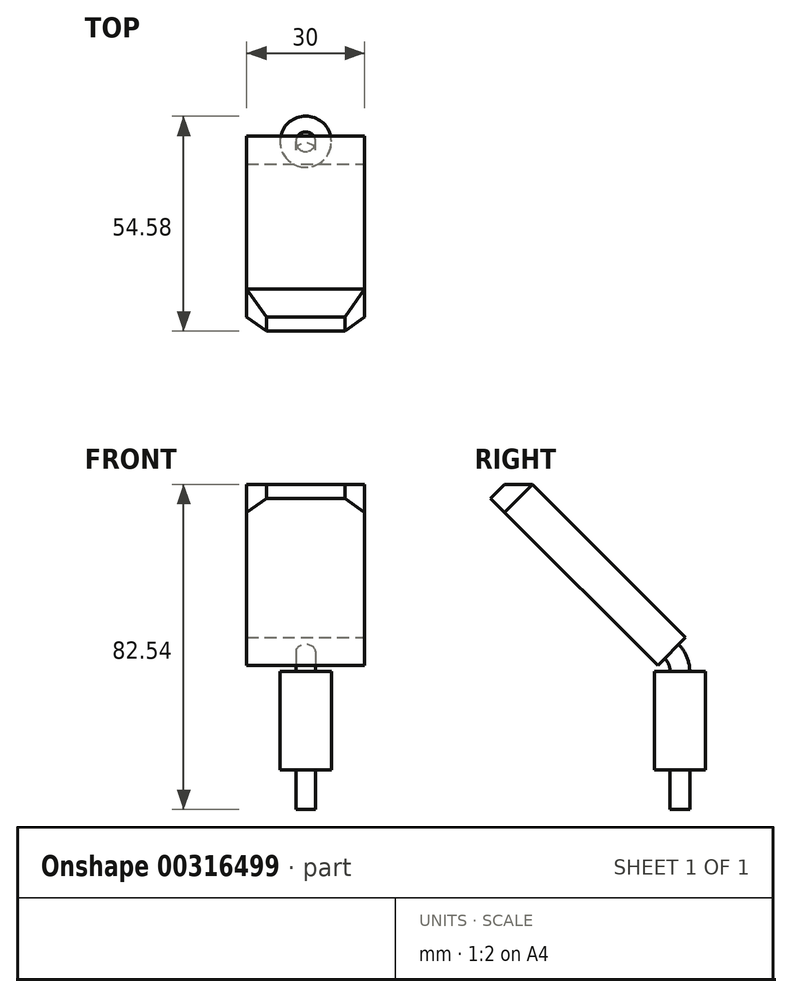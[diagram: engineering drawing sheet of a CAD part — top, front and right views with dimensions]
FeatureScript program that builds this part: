
annotation { "Feature Type Name" : "Feature", "Feature Type Description" : "" }
export const myFeature = defineFeature(function(context is Context, id is Id, definition is map)
    precondition{}
    {
        {
            var Q0;
            Q0=qCreatedBy(makeId("Top.planeOp"),FACE);
            var sketch = newSketch(context, id + "F0", { "sketchPlane" : qUnion([Q0])});
            skCircle(sketch, "E0", {"center": v(0, 0) * mm, "radius": 2.5 * mm});
            skSolve(sketch);
        }
        {
            var Q0;
            Q0=makeQuery(id+"F0.imprint","IMPRINT",FACE,{"disambiguationData":[TD([[makeQuery(id+"F0.imprint","IMPRINT",EDGE,{"derivedFrom":sQuery(id+"F0.wireOp",EDGE,"E0")}),1.0]])]});
            extrude(context, id + "F1", {"entities" : qUnion([Q0]), "depth" : 10 * mm});
        }
        {
            var Q0;
            Q0=makeQuery(id+"F1.opExtrude","CAP_FACE",FACE,{"disambiguationData":[OSD([sQuery(id+"F0.wireOp",EDGE,"E0")])],"isStart":false});
            var sketch = newSketch(context, id + "F2", { "sketchPlane" : qUnion([Q0])});
            skCircle(sketch, "E1", {"center": v(0, 0) * mm, "radius": 6.5 * mm});
            skSolve(sketch);
        }
        {
            var Q0;
            Q0=makeQuery(id+"F2.imprint","IMPRINT",FACE,{"disambiguationData":[TD([[makeQuery(id+"F2.imprint","IMPRINT",EDGE,{"derivedFrom":makeQuery(id+"F1.opExtrude","CAP_EDGE",EDGE,{"disambiguationData":[OSD([sQuery(id+"F0.wireOp",EDGE,"E0")])],"isStart":false})}),1.0]])]});
            var Q1;
            Q1=makeQuery(id+"F2.imprint","IMPRINT",FACE,{"disambiguationData":[TD([[makeQuery(id+"F2.imprint","IMPRINT",EDGE,{"derivedFrom":sQuery(id+"F2.wireOp",EDGE,"E1")}),1.0]])]});
            extrude(context, id + "F3", {"entities" : qUnion([Q0, Q1]), "operationType" : NewBodyOperationType.ADD, "depth" : 25 * mm});
        }
        {
            var Q0;
            Q0=makeQuery(id+"F3.opExtrude","CAP_FACE",FACE,{"disambiguationData":[OSD([sQuery(id+"F2.wireOp",EDGE,"E1")])],"isStart":false});
            var sketch = newSketch(context, id + "F4", { "sketchPlane" : qUnion([Q0])});
            skCircle(sketch, "E2", {"center": v(0, 0) * mm, "radius": 2.5 * mm});
            skLineSegment(sketch, "E3", {"start": v(-2.34, -7.23) * mm, "end": v(5.9, -7.23) * mm});
            skSolve(sketch);
        }
        {
            var Q0;
            Q0=makeQuery(id+"F4.imprint","IMPRINT",FACE,{"disambiguationData":[TD([[makeQuery(id+"F4.imprint","IMPRINT",EDGE,{"derivedFrom":sQuery(id+"F4.wireOp",EDGE,"E2")}),1.0]])]});
            var Q1;
            Q1=sQuery(id+"F4.wireOp",EDGE,"E3");
            revolve(context, id + "F5", {"operationType" : NewBodyOperationType.ADD, "entities" : qUnion([Q0]), "axis" : qUnion([Q1]), "revolveType" : RevolveType.ONE_DIRECTION, "angle" : 45 * degree});
        }
        {
            var Q0;
            Q0=makeQuery(id+"F5.opRevolve","CAP_FACE",FACE,{"disambiguationData":[OSD([sQuery(id+"F4.wireOp",EDGE,"E2")])],"isStart":false});
            var sketch = newSketch(context, id + "F6", { "sketchPlane" : qUnion([Q0])});
            skLineSegment(sketch, "E4.bottom", {"start": v(-15, 31.87) * mm, "end": v(15, 31.87) * mm});
            skLineSegment(sketch, "E4.top", {"start": v(-15, 21.87) * mm, "end": v(15, 21.87) * mm});
            skLineSegment(sketch, "E4.left", {"start": v(-15, 31.87) * mm, "end": v(-15, 21.87) * mm});
            skLineSegment(sketch, "E4.right", {"start": v(15, 31.87) * mm, "end": v(15, 21.87) * mm});
            skPoint(sketch, "E4.middle", {"position": v(0, 26.87) * mm});
            skSolve(sketch);
        }
        {
            var Q0;
            Q0=makeQuery(id+"F6.imprint","IMPRINT",FACE,{"disambiguationData":[TD([[makeQuery(id+"F6.imprint","IMPRINT",EDGE,{"derivedFrom":makeQuery(id+"F5.opRevolve","CAP_EDGE",EDGE,{"disambiguationData":[OSD([sQuery(id+"F4.wireOp",EDGE,"E2")])],"isStart":false})}),1.0]])]});
            var Q1;
            Q1=makeQuery(id+"F6.imprint","IMPRINT",FACE,{"disambiguationData":[TD([[makeQuery(id+"F6.imprint","IMPRINT",EDGE,{"derivedFrom":sQuery(id+"F6.wireOp",EDGE,"E4.bottom")}),-1.0]])]});
            extrude(context, id + "F7", {"entities" : qUnion([Q0, Q1]), "operationType" : NewBodyOperationType.ADD, "depth" : 60 * mm});
        }
        {
            var Q0;
            Q0=makeQuery(id+"F7.opExtrude","CAP_EDGE",EDGE,{"disambiguationData":[OSD([sQuery(id+"F6.wireOp",EDGE,"E4.bottom")])],"isStart":false});
            var Q1;
            Q1=makeQuery(id+"F7.opExtrude","CAP_EDGE",EDGE,{"disambiguationData":[OSD([sQuery(id+"F6.wireOp",EDGE,"E4.left")])],"isStart":false});
            var Q2;
            Q2=makeQuery(id+"F7.opExtrude","CAP_EDGE",EDGE,{"disambiguationData":[OSD([sQuery(id+"F6.wireOp",EDGE,"E4.right")])],"isStart":false});
            chamfer(context, id + "F8", {"entities" : qUnion([Q0, Q1, Q2]), "chamferType" : ChamferType.OFFSET_ANGLE, "width" : 5 * mm, "oppositeDirection" : false, "angle" : 45 * degree, "tangentPropagation" : true});
        }
    });
